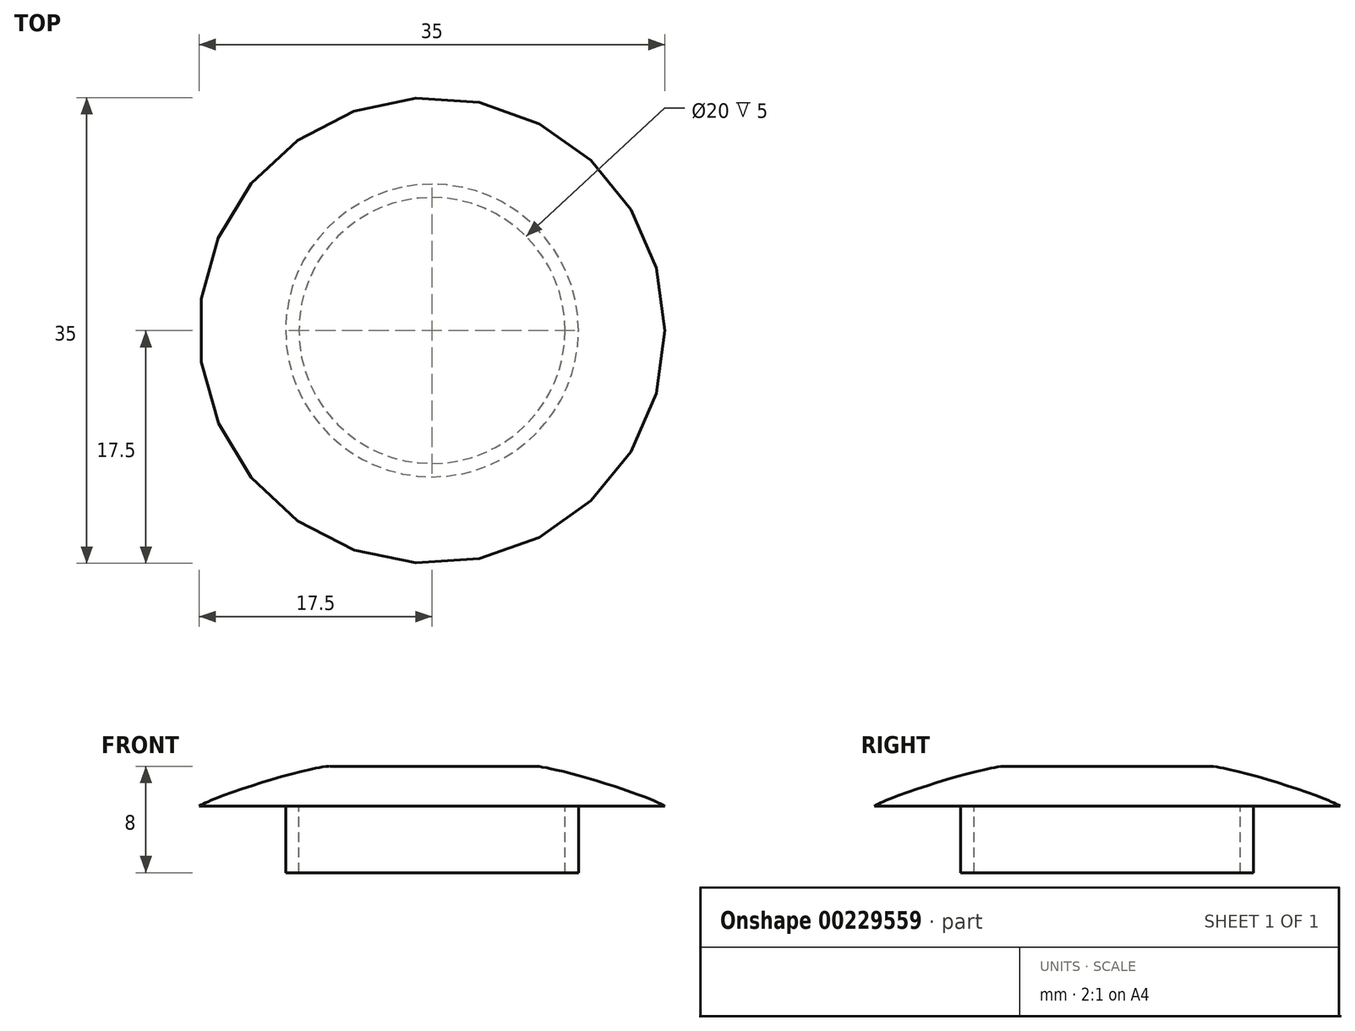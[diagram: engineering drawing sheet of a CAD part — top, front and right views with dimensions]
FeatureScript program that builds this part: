
annotation { "Feature Type Name" : "Feature", "Feature Type Description" : "" }
export const myFeature = defineFeature(function(context is Context, id is Id, definition is map)
    precondition{}
    {
        {
            var Q0;
            Q0=qCreatedBy(makeId("Top.planeOp"),FACE);
            var sketch = newSketch(context, id + "F0", { "sketchPlane" : qUnion([Q0])});
            skCircle(sketch, "E0", {"center": v(0, 0) * mm, "radius": 17.5 * mm});
            skCircle(sketch, "E1", {"center": v(0, 0) * mm, "radius": 11 * mm});
            skCircle(sketch, "E2", {"center": v(0, 0) * mm, "radius": 10 * mm});
            skSolve(sketch);
        }
        {
            var Q0;
            Q0=makeQuery(id+"F0.imprint","IMPRINT",FACE,{"disambiguationData":[TD([[makeQuery(id+"F0.imprint","IMPRINT",EDGE,{"derivedFrom":sQuery(id+"F0.wireOp",EDGE,"E0")}),1.0]])]});
            var Q1;
            Q1=makeQuery(id+"F0.imprint","IMPRINT",FACE,{"disambiguationData":[TD([[makeQuery(id+"F0.imprint","IMPRINT",EDGE,{"derivedFrom":sQuery(id+"F0.wireOp",EDGE,"E2")}),1.0]])]});
            var Q2;
            Q2=makeQuery(id+"F0.imprint","IMPRINT",FACE,{"disambiguationData":[TD([[makeQuery(id+"F0.imprint","IMPRINT",EDGE,{"derivedFrom":sQuery(id+"F0.wireOp",EDGE,"E1")}),1.0]])]});
            extrude(context, id + "F1", {"entities" : qUnion([Q0, Q1, Q2]), "depth" : 3 * mm});
        }
        {
            var Q0;
            Q0=makeQuery(id+"F0.imprint","IMPRINT",FACE,{"disambiguationData":[TD([[makeQuery(id+"F0.imprint","IMPRINT",EDGE,{"derivedFrom":sQuery(id+"F0.wireOp",EDGE,"E0")}),1.0]])]});
            var sketch = newSketch(context, id + "F2", { "sketchPlane" : qUnion([Q0])});
            skCircle(sketch, "E3", {"center": v(0, 0) * mm, "radius": 11 * mm});
            skCircle(sketch, "E4", {"center": v(0, 0) * mm, "radius": 10 * mm});
            skSolve(sketch);
        }
        {
            var Q0;
            Q0 = qSketchRegion(id + "F2", true);
            var Q1;
            Q1=sQuery(id+"F2.wireOp",EDGE,"E3");
            extrude(context, id + "F3", {"entities" : qUnion([Q0]), "surfaceEntities" : qUnion([Q1]), "oppositeDirection" : true, "depth" : 5 * mm});
        }
        {
            var Q0;
            Q0=makeQuery(id+"F1.opExtrude","CAP_EDGE",EDGE,{"disambiguationData":[OSD([sQuery(id+"F0.wireOp",EDGE,"E0")])],"isStart":false});
            fillet(context, id + "F4", {"entities" : qUnion([Q0]), "radius" : 17.4 * mm, "tangentPropagation" : true, "rho" : 0.2, "crossSection" : FilletCrossSection.CONIC, "allowEdgeOverflow" : false});
        }
    });
